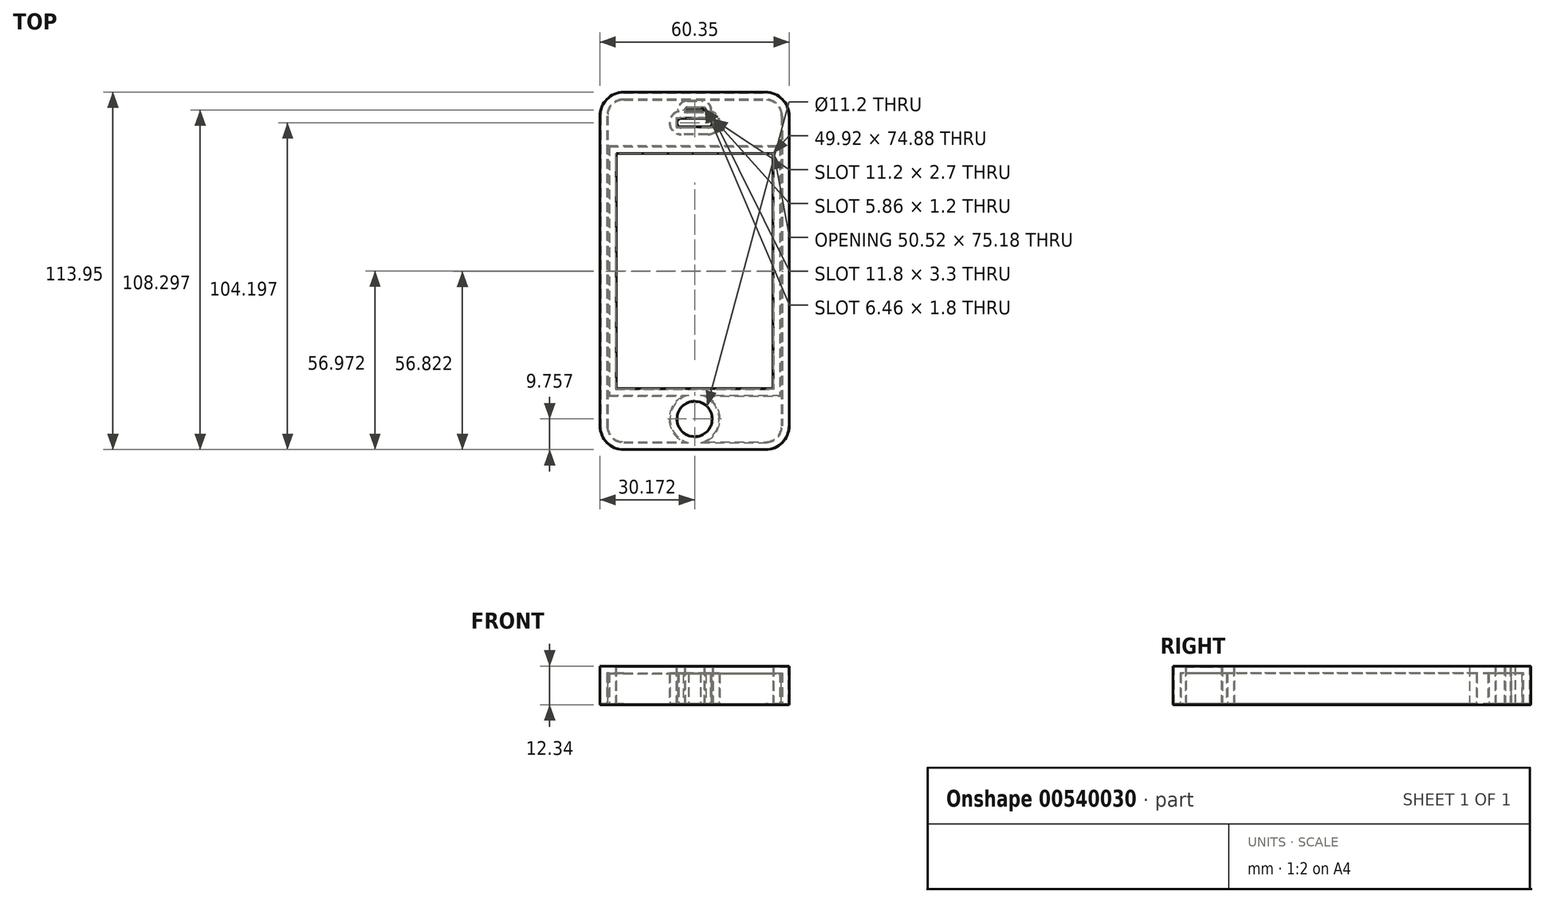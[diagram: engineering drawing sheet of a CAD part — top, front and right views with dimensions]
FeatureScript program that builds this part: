
annotation { "Feature Type Name" : "Feature", "Feature Type Description" : "" }
export const myFeature = defineFeature(function(context is Context, id is Id, definition is map)
    precondition{}
    {
        {
            var Q0;
            Q0=qCreatedBy(makeId("Top.planeOp"),FACE);
            var sketch = newSketch(context, id + "F0", { "sketchPlane" : qUnion([Q0])});
            skLineSegment(sketch, "E0.bottom", {"start": v(-39.51, 40.58) * mm, "end": v(5.7, 40.58) * mm});
            skLineSegment(sketch, "E0.top", {"start": v(-39.51, -73.37) * mm, "end": v(5.7, -73.37) * mm});
            skLineSegment(sketch, "E0.left", {"start": v(-47.08, 33) * mm, "end": v(-47.08, -65.8) * mm});
            skLineSegment(sketch, "E0.right", {"start": v(13.27, 33) * mm, "end": v(13.27, -65.8) * mm});
            skPoint(sketch, "E0.middle", {"position": v(-16.9, -16.4) * mm});
            skPoint(sketch, "E1.visualSharp", {"position": v(-47.08, 40.58) * mm});
            skArc(sketch, "E1.filletArc", {"start": v(-39.51, 40.58) * mm, "mid": v(-44.87, 38.36) * mm, "end": v(-47.08, 33) * mm});
            skPoint(sketch, "E2.visualSharp", {"position": v(13.27, 40.58) * mm});
            skArc(sketch, "E2.filletArc", {"start": v(13.27, 33) * mm, "mid": v(11.05, 38.36) * mm, "end": v(5.7, 40.58) * mm});
            skPoint(sketch, "E3.visualSharp", {"position": v(-47.08, -73.37) * mm});
            skArc(sketch, "E3.filletArc", {"start": v(-47.08, -65.8) * mm, "mid": v(-44.87, -71.16) * mm, "end": v(-39.51, -73.37) * mm});
            skPoint(sketch, "E4.visualSharp", {"position": v(13.27, -73.37) * mm});
            skArc(sketch, "E4.filletArc", {"start": v(5.7, -73.37) * mm, "mid": v(11.05, -71.16) * mm, "end": v(13.27, -65.8) * mm});
            skCircle(sketch, "E5", {"center": v(-16.9, -63.61) * mm, "radius": 5.6 * mm});
            skLineSegment(sketch, "E6.bottom", {"start": v(-12.66, 29.48) * mm, "end": v(-21.16, 29.48) * mm});
            skLineSegment(sketch, "E6.top", {"start": v(-12.66, 32.18) * mm, "end": v(-21.16, 32.18) * mm});
            skLineSegment(sketch, "E6.left", {"start": v(-11.3, 30.83) * mm, "end": v(-11.3, 30.83) * mm});
            skLineSegment(sketch, "E6.right", {"start": v(-22.5, 30.83) * mm, "end": v(-22.5, 30.83) * mm});
            skPoint(sketch, "E6.middle", {"position": v(-16.9, 30.83) * mm});
            skPoint(sketch, "E7.visualSharp", {"position": v(-22.5, 32.18) * mm});
            skArc(sketch, "E7.filletArc", {"start": v(-21.16, 32.18) * mm, "mid": v(-22.11, 31.78) * mm, "end": v(-22.5, 30.83) * mm});
            skPoint(sketch, "E8.visualSharp", {"position": v(-22.5, 29.48) * mm});
            skArc(sketch, "E8.filletArc", {"start": v(-22.5, 30.83) * mm, "mid": v(-22.11, 29.87) * mm, "end": v(-21.16, 29.48) * mm});
            skPoint(sketch, "E9.visualSharp", {"position": v(-11.3, 29.48) * mm});
            skArc(sketch, "E9.filletArc", {"start": v(-12.66, 29.48) * mm, "mid": v(-11.7, 29.87) * mm, "end": v(-11.3, 30.83) * mm});
            skPoint(sketch, "E10.visualSharp", {"position": v(-11.3, 32.18) * mm});
            skArc(sketch, "E10.filletArc", {"start": v(-11.3, 30.83) * mm, "mid": v(-11.7, 31.78) * mm, "end": v(-12.66, 32.18) * mm});
            skPoint(sketch, "E11.endSnap0", {"position": v(-16.9, 29.48) * mm});
            skPoint(sketch, "E12.middle", {"position": v(-16.9, 34.93) * mm});
            skLineSegment(sketch, "E13.left", {"start": v(-13.98, 34.93) * mm, "end": v(-13.98, 34.93) * mm});
            skLineSegment(sketch, "E14.MirrorCS", {"start": v(-19.84, 34.93) * mm, "end": v(-19.84, 34.93) * mm});
            skLineSegment(sketch, "E15", {"start": v(-19.24, 35.53) * mm, "end": v(-14.58, 35.53) * mm});
            skLineSegment(sketch, "E16", {"start": v(-14.58, 34.33) * mm, "end": v(-19.24, 34.33) * mm});
            skPoint(sketch, "E17.visualSharp", {"position": v(-19.84, 35.53) * mm});
            skArc(sketch, "E17.filletArc", {"start": v(-19.24, 35.53) * mm, "mid": v(-19.66, 35.35) * mm, "end": v(-19.84, 34.93) * mm});
            skPoint(sketch, "E18.visualSharp", {"position": v(-19.84, 34.33) * mm});
            skArc(sketch, "E18.filletArc", {"start": v(-19.84, 34.93) * mm, "mid": v(-19.66, 34.5) * mm, "end": v(-19.24, 34.33) * mm});
            skPoint(sketch, "E19.visualSharp", {"position": v(-13.98, 35.53) * mm});
            skArc(sketch, "E19.filletArc", {"start": v(-13.98, 34.93) * mm, "mid": v(-14.15, 35.35) * mm, "end": v(-14.58, 35.53) * mm});
            skPoint(sketch, "E20.visualSharp", {"position": v(-13.98, 34.33) * mm});
            skArc(sketch, "E20.filletArc", {"start": v(-14.58, 34.33) * mm, "mid": v(-14.15, 34.5) * mm, "end": v(-13.98, 34.93) * mm});
            skLineSegment(sketch, "E21.bottom", {"start": v(-41.87, 21.04) * mm, "end": v(8.05, 21.04) * mm});
            skLineSegment(sketch, "E21.top", {"start": v(-41.87, -53.84) * mm, "end": v(8.05, -53.84) * mm});
            skLineSegment(sketch, "E21.left", {"start": v(-41.87, 21.04) * mm, "end": v(-41.87, -53.84) * mm});
            skLineSegment(sketch, "E21.right", {"start": v(8.05, 21.04) * mm, "end": v(8.05, -53.84) * mm});
            skSolve(sketch);
        }
        {
            var Q0;
            Q0=makeQuery(id+"F0.imprint","IMPRINT",FACE,{"disambiguationData":[TD([[makeQuery(id+"F0.imprint","IMPRINT",EDGE,{"derivedFrom":sQuery(id+"F0.wireOp",EDGE,"E0.bottom")}),-1.0]])]});
            extrude(context, id + "F1", {"entities" : qUnion([Q0]), "depth" : 12.34 * mm, "offsetDistance" : 25 * mm});
        }
        {
            var Q0;
            Q0=makeQuery(id+"F1.opExtrude","CAP_FACE",FACE,{"disambiguationData":[OSD([sQuery(id+"F0.wireOp",EDGE,"E0.bottom"),sQuery(id+"F0.wireOp",EDGE,"E0.top"),sQuery(id+"F0.wireOp",EDGE,"E0.left"),sQuery(id+"F0.wireOp",EDGE,"E0.right"),sQuery(id+"F0.wireOp",EDGE,"E1.filletArc"),sQuery(id+"F0.wireOp",EDGE,"E2.filletArc"),sQuery(id+"F0.wireOp",EDGE,"E3.filletArc"),sQuery(id+"F0.wireOp",EDGE,"E4.filletArc"),sQuery(id+"F0.wireOp",EDGE,"E5"),sQuery(id+"F0.wireOp",EDGE,"E6.bottom"),sQuery(id+"F0.wireOp",EDGE,"E6.top"),sQuery(id+"F0.wireOp",EDGE,"E7.filletArc"),sQuery(id+"F0.wireOp",EDGE,"E8.filletArc"),sQuery(id+"F0.wireOp",EDGE,"E9.filletArc"),sQuery(id+"F0.wireOp",EDGE,"E10.filletArc"),sQuery(id+"F0.wireOp",EDGE,"E15"),sQuery(id+"F0.wireOp",EDGE,"E16"),sQuery(id+"F0.wireOp",EDGE,"E17.filletArc"),sQuery(id+"F0.wireOp",EDGE,"E18.filletArc"),sQuery(id+"F0.wireOp",EDGE,"E19.filletArc"),sQuery(id+"F0.wireOp",EDGE,"E20.filletArc"),sQuery(id+"F0.wireOp",EDGE,"E21.bottom"),sQuery(id+"F0.wireOp",EDGE,"E21.top"),sQuery(id+"F0.wireOp",EDGE,"E21.left"),sQuery(id+"F0.wireOp",EDGE,"E21.right")])],"isStart":true});
            shell(context, id + "F2", {"entities" : qUnion([Q0]), "thickness" : 2.5 * mm});
        }
        {
            var Q0;
            Q0=makeQuery(id+"F1.opExtrude","SWEPT_FACE",FACE,{"disambiguationData":[OSD([sQuery(id+"F0.wireOp",EDGE,"E21.bottom")])]});
            shell(context, id + "F3", {"entities" : qUnion([Q0]), "thickness" : 0.3 * mm});
        }
    });
